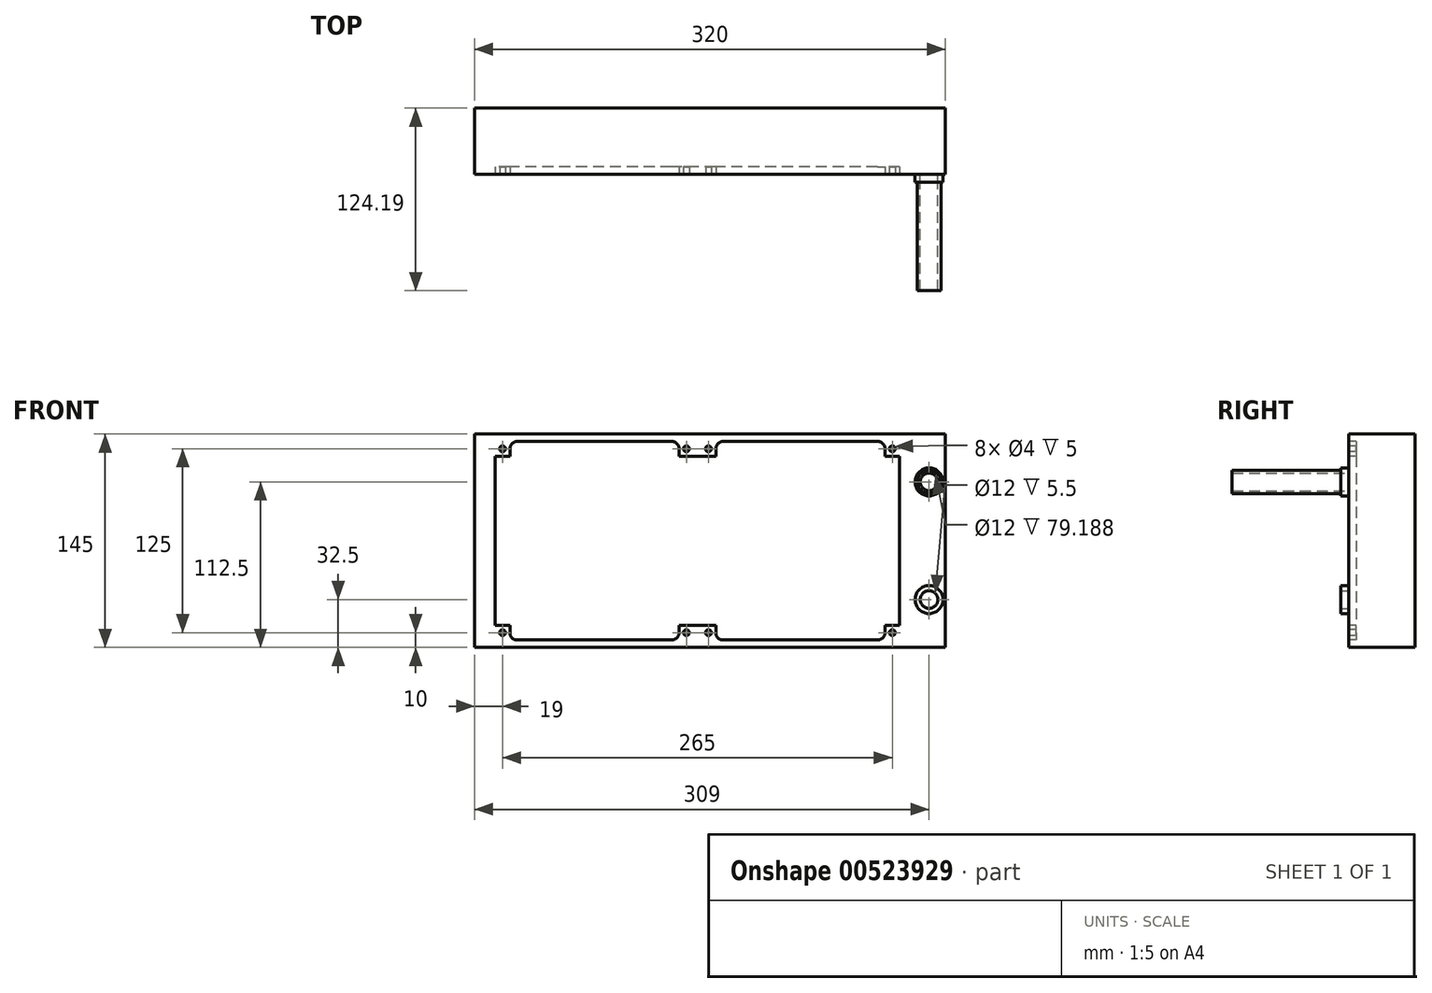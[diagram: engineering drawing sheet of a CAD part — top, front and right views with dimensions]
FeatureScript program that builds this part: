
annotation { "Feature Type Name" : "Feature", "Feature Type Description" : "" }
export const myFeature = defineFeature(function(context is Context, id is Id, definition is map)
    precondition{}
    {
        {
            var Q0;
            Q0=qCreatedBy(makeId("Front.planeOp"),FACE);
            var sketch = newSketch(context, id + "F0", { "sketchPlane" : qUnion([Q0])});
            skLineSegment(sketch, "E0.bottom", {"start": v(0, 72.5) * mm, "end": v(320, 72.5) * mm});
            skLineSegment(sketch, "E0.top", {"start": v(0, -72.5) * mm, "end": v(320, -72.5) * mm});
            skLineSegment(sketch, "E0.left", {"start": v(0, 72.5) * mm, "end": v(0, -72.5) * mm});
            skLineSegment(sketch, "E0.right", {"start": v(320, 72.5) * mm, "end": v(320, -72.5) * mm});
            skSolve(sketch);
        }
        {
            var Q0;
            Q0=qSketchRegion(id+"F0",true);
            extrude(context, id + "F1", {"entities" : qUnion([Q0]), "depth" : 45 * mm});
        }
        {
            var Q0;
            Q0=makeQuery(id+"F1.opExtrude","CAP_FACE",FACE,{"disambiguationData":[OSD([sQuery(id+"F0.wireOp",EDGE,"E0.bottom"),sQuery(id+"F0.wireOp",EDGE,"E0.top"),sQuery(id+"F0.wireOp",EDGE,"E0.left"),sQuery(id+"F0.wireOp",EDGE,"E0.right")])],"isStart":false});
            var sketch = newSketch(context, id + "F2", { "sketchPlane" : qUnion([Q0])});
            skCircle(sketch, "E1", {"center": v(309, -40) * mm, "radius": 9.5 * mm});
            skCircle(sketch, "E2", {"center": v(309, 40) * mm, "radius": 9.5 * mm});
            skLineSegment(sketch, "E3", {"start": v(0, 0) * mm, "end": v(320, 0) * mm, "construction": true});
            skCircle(sketch, "E4", {"center": v(309, 40) * mm, "radius": 6 * mm});
            skCircle(sketch, "E5", {"center": v(309, -40) * mm, "radius": 6 * mm});
            skSolve(sketch);
        }
        {
            var Q0;
            Q0=qSketchRegion(id+"F2",true);
            extrude(context, id + "F3", {"entities" : qUnion([Q0]), "operationType" : NewBodyOperationType.ADD, "depth" : 5.5 * mm});
        }
        {
            var Q0;
            {var subQ0=sQuery(id+"F0.wireOp",EDGE,"E0.right");var subQ1=sQuery(id+"F0.wireOp",EDGE,"E0.left");var subQ2=sQuery(id+"F0.wireOp",EDGE,"E0.top");var subQ3=sQuery(id+"F0.wireOp",EDGE,"E0.bottom");Q0=makeQuery(id+"F3.boolean.opBoolean","SPLIT",FACE,{"disambiguationData":[TD([makeQuery(id+"F1.opExtrude","SWEPT_FACE",FACE,{"disambiguationData":[OSD([subQ3])]})])],"derivedFrom":makeQuery(id+"F1.opExtrude","CAP_FACE",FACE,{"disambiguationData":[OSD([subQ3,subQ2,subQ1,subQ0])],"isStart":false})});}
            var sketch = newSketch(context, id + "F4", { "sketchPlane" : qUnion([Q0])});
            skCircle(sketch, "E6", {"center": v(19, 62.5) * mm, "radius": 2 * mm});
            skCircle(sketch, "E7", {"center": v(144, 62.5) * mm, "radius": 2 * mm});
            skCircle(sketch, "E8", {"center": v(159, 62.5) * mm, "radius": 2 * mm});
            skCircle(sketch, "E9", {"center": v(284, 62.5) * mm, "radius": 2 * mm});
            skLineSegment(sketch, "E10", {"start": v(14, 57.5) * mm, "end": v(14, 0) * mm});
            skLineSegment(sketch, "E11", {"start": v(289, 0) * mm, "end": v(289, 57.5) * mm});
            skLineSegment(sketch, "E12", {"start": v(289, 57.5) * mm, "end": v(279, 57.5) * mm});
            skLineSegment(sketch, "E13", {"start": v(279, 57.5) * mm, "end": v(279, 62.5) * mm});
            skLineSegment(sketch, "E14", {"start": v(274, 67.5) * mm, "end": v(169, 67.5) * mm});
            skLineSegment(sketch, "E15", {"start": v(164, 62.5) * mm, "end": v(164, 57.5) * mm});
            skLineSegment(sketch, "E16", {"start": v(164, 57.5) * mm, "end": v(139, 57.5) * mm});
            skLineSegment(sketch, "E17", {"start": v(139, 57.5) * mm, "end": v(139, 62.5) * mm});
            skLineSegment(sketch, "E18", {"start": v(134, 67.5) * mm, "end": v(29, 67.5) * mm});
            skLineSegment(sketch, "E19", {"start": v(24, 62.5) * mm, "end": v(24, 57.5) * mm});
            skLineSegment(sketch, "E20", {"start": v(24, 57.5) * mm, "end": v(14, 57.5) * mm});
            skLineSegment(sketch, "E21", {"start": v(0, 0) * mm, "end": v(320, 0) * mm, "construction": true});
            skPoint(sketch, "E22.visualSharp", {"position": v(164, 67.5) * mm});
            skArc(sketch, "E22.filletArc", {"start": v(169, 67.5) * mm, "mid": v(165.46, 66.04) * mm, "end": v(164, 62.5) * mm});
            skPoint(sketch, "E23.visualSharp", {"position": v(139, 67.5) * mm});
            skArc(sketch, "E23.filletArc", {"start": v(139, 62.5) * mm, "mid": v(137.54, 66.04) * mm, "end": v(134, 67.5) * mm});
            skPoint(sketch, "E24.visualSharp", {"position": v(279, 67.5) * mm});
            skArc(sketch, "E24.filletArc", {"start": v(279, 62.5) * mm, "mid": v(277.54, 66.04) * mm, "end": v(274, 67.5) * mm});
            skPoint(sketch, "E25.visualSharp", {"position": v(24, 67.5) * mm});
            skArc(sketch, "E25.filletArc", {"start": v(29, 67.5) * mm, "mid": v(25.46, 66.04) * mm, "end": v(24, 62.5) * mm});
            skCircle(sketch, "E26.MirrorC", {"center": v(284, -62.5) * mm, "radius": 2 * mm});
            skLineSegment(sketch, "E27.MirrorCS", {"start": v(289, 0) * mm, "end": v(289, -57.5) * mm});
            skLineSegment(sketch, "E28.MirrorCS", {"start": v(289, -57.5) * mm, "end": v(279, -57.5) * mm});
            skLineSegment(sketch, "E29.MirrorCS", {"start": v(279, -57.5) * mm, "end": v(279, -62.5) * mm});
            skArc(sketch, "E30.MirrorCS", {"start": v(279, -62.5) * mm, "mid": v(277.54, -66.04) * mm, "end": v(274, -67.5) * mm});
            skLineSegment(sketch, "E31.MirrorCS", {"start": v(274, -67.5) * mm, "end": v(169, -67.5) * mm});
            skArc(sketch, "E32.MirrorCS", {"start": v(169, -67.5) * mm, "mid": v(165.46, -66.04) * mm, "end": v(164, -62.5) * mm});
            skLineSegment(sketch, "E33.MirrorCS", {"start": v(164, -62.5) * mm, "end": v(164, -57.5) * mm});
            skCircle(sketch, "E34.MirrorC", {"center": v(159, -62.5) * mm, "radius": 2 * mm});
            skCircle(sketch, "E35.MirrorC", {"center": v(144, -62.5) * mm, "radius": 2 * mm});
            skLineSegment(sketch, "E36.MirrorCS", {"start": v(164, -57.5) * mm, "end": v(139, -57.5) * mm});
            skCircle(sketch, "E37.MirrorC", {"center": v(19, -62.5) * mm, "radius": 2 * mm});
            skLineSegment(sketch, "E38.MirrorCS", {"start": v(139, -57.5) * mm, "end": v(139, -62.5) * mm});
            skArc(sketch, "E39.MirrorCS", {"start": v(139, -62.5) * mm, "mid": v(137.54, -66.04) * mm, "end": v(134, -67.5) * mm});
            skLineSegment(sketch, "E40.MirrorCS", {"start": v(134, -67.5) * mm, "end": v(29, -67.5) * mm});
            skArc(sketch, "E41.MirrorCS", {"start": v(29, -67.5) * mm, "mid": v(25.46, -66.04) * mm, "end": v(24, -62.5) * mm});
            skLineSegment(sketch, "E42.MirrorCS", {"start": v(24, -62.5) * mm, "end": v(24, -57.5) * mm});
            skLineSegment(sketch, "E43.MirrorCS", {"start": v(14, -57.5) * mm, "end": v(14, 0) * mm});
            skLineSegment(sketch, "E44.MirrorCS", {"start": v(24, -57.5) * mm, "end": v(14, -57.5) * mm});
            skSolve(sketch);
        }
        {
            var Q0;
            Q0=qSketchRegion(id+"F4",true);
            extrude(context, id + "F5", {"entities" : qUnion([Q0]), "operationType" : NewBodyOperationType.REMOVE, "oppositeDirection" : true, "depth" : 5 * mm});
        }
        {
            var Q0;
            {var subQ0=sQuery(id+"F0.wireOp",EDGE,"E0.right");var subQ1=sQuery(id+"F0.wireOp",EDGE,"E0.left");var subQ2=sQuery(id+"F0.wireOp",EDGE,"E0.top");var subQ3=sQuery(id+"F0.wireOp",EDGE,"E0.bottom");Q0=makeQuery(id+"F3.boolean.opBoolean","SPLIT",FACE,{"disambiguationData":[TD([makeQuery(id+"F1.opExtrude","SWEPT_FACE",FACE,{"disambiguationData":[OSD([subQ3])]})])],"derivedFrom":makeQuery(id+"F1.opExtrude","CAP_FACE",FACE,{"disambiguationData":[OSD([subQ3,subQ2,subQ1,subQ0])],"isStart":false})});}
            cPlane(context, id + "F6", {"entities" : qUnion([Q0]), "cplaneType" : CPlaneType.OFFSET, "offset" : (45 / 2) * mm, "oppositeDirection" : true, "width" : 150 * mm, "height" : 150 * mm});
        }
        {
            var Q0;
            Q0=makeQuery(id+"F3.opExtrude","CAP_FACE",FACE,{"disambiguationData":[OSD([sQuery(id+"F2.wireOp",EDGE,"E2"),sQuery(id+"F2.wireOp",EDGE,"E4")])],"isStart":false});
            var sketch = newSketch(context, id + "F7", { "sketchPlane" : qUnion([Q0])});
            skCircle(sketch, "E45", {"center": v(309, 40) * mm, "radius": 6 * mm});
            skCircle(sketch, "E46", {"center": v(309, 40) * mm, "radius": 8 * mm});
            skSolve(sketch);
        }
        {
            var Q0;
            Q0=qSketchRegion(id+"F7",true);
            extrude(context, id + "F8", {"entities" : qUnion([Q0]), "operationType" : NewBodyOperationType.ADD, "depth" : 73.69 * mm});
        }
    });
